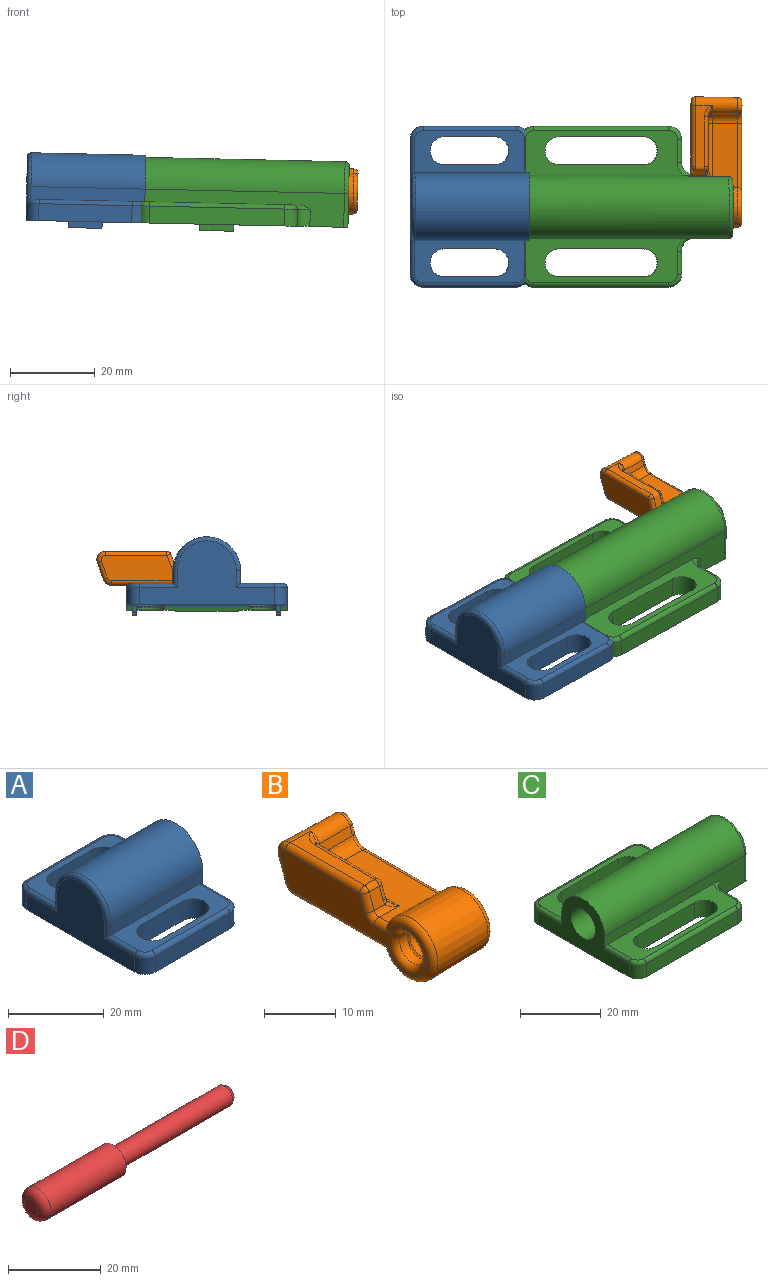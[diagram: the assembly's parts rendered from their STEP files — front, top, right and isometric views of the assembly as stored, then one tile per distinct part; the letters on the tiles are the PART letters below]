
ASSEMBLY  parts=4 mates=3
PART A: 46 faces, bbox 28.5x38.5x18.2 mm
  f0: plane 38x28mm, normal (0,0,-1), area 814.3mm2, adj f3,f4,f8,f9,f13,f14,f15,f16
  f1: plane 26x10mm, normal (0,0,1), area 144.9mm2, adj f5,f17,f18,f19,f20,f25,f26,f28
  f2: plane 26x10mm, normal (0,0,1), area 144.9mm2, adj f7,f13,f14,f15,f16,f27,f29,f31
  f3: plane 32x16mm, normal (1,0,0), area 215.6mm2, adj f0,f5,f6,f7,f12,f21,f23,f25
  f4: plane 22x4mm, normal (0,-1,0), area 88mm2, adj f0,f21,f22,f28
  f5: plane 27x4mm, normal (0,-1,0), area 81.2mm2, adj f1,f3,f6,f25,f34
  f6: cylinder r=8mm len=27mm, axis (1,0,0), area 678.6mm2, adj f3,f5,f7,f36
  f7: plane 27x4mm, normal (0,1,0), area 81.2mm2, adj f2,f3,f6,f27,f37
  f8: plane 22x4mm, normal (0,1,0), area 88mm2, adj f0,f23,f24,f31
  f9: plane 32x15mm, normal (-1,0,0), area 261mm2, adj f0,f22,f24,f32,f34,f35,f36,f37
  f10: plane 8.7x8.7mm, normal (1,0,0), area 59.4mm2, adj f11
  f11: cylinder r=4.35mm len=23.4mm, axis (1,0,0), area 639.6mm2, adj f10,f12
  f12: cone r=4.35mm half-angle=45deg, axis (1,0,0), area 24.8mm2, adj f3,f11
  f13: cylinder r=3.3mm len=6.6mm, axis (0,0,-1), area 51.8mm2, adj f0,f2,f14,f16
  f14: plane 12x5mm, normal (0,1,0), area 60mm2, adj f0,f2,f13,f15
  f15: cylinder r=3.3mm len=6.6mm, axis (0,0,-1), area 51.8mm2, adj f0,f2,f14,f16
  f16: plane 12x6.5mm, normal (0,-1,0), area 72mm2, adj f0,f2,f13,f15,f38,f39,f41
  f17: cylinder r=3.3mm len=6.6mm, axis (0,0,-1), area 51.8mm2, adj f0,f1,f18,f20
  f18: plane 12x6.5mm, normal (0,1,0), area 72mm2, adj f0,f1,f17,f19,f43,f44,f45
  f19: cylinder r=3.3mm len=6.6mm, axis (0,0,-1), area 51.8mm2, adj f0,f1,f18,f20
  f20: plane 12x5mm, normal (0,-1,0), area 60mm2, adj f0,f1,f17,f19
  f21: cylinder r=3mm len=4mm, axis (0,0,-1), area 18.8mm2, adj f0,f3,f4,f26
  f22: cylinder r=3mm len=4mm, axis (0,0,1), area 18.8mm2, adj f0,f4,f9,f30
  f23: cylinder r=3mm len=4mm, axis (0,0,1), area 18.8mm2, adj f0,f3,f8,f29
  f24: cylinder r=3mm len=4mm, axis (0,0,-1), area 18.8mm2, adj f0,f8,f9,f33
  f25: cylinder r=1mm len=8mm, axis (0,-1,0), area 12.6mm2, adj f1,f3,f5,f26
  f26: torus R=2mm, axis (0,0,1), area 6.5mm2, adj f1,f21,f25,f28
  f27: cylinder r=1mm len=8mm, axis (0,-1,0), area 12.6mm2, adj f2,f3,f7,f29
  f28: cylinder r=1mm len=22mm, axis (1,0,0), area 34.6mm2, adj f1,f4,f26,f30
  f29: torus R=2mm, axis (0,0,1), area 6.5mm2, adj f2,f23,f27,f31
  f30: torus R=2mm, axis (0,0,1), area 6.5mm2, adj f1,f22,f28,f32
  f31: cylinder r=1mm len=22mm, axis (1,0,0), area 34.6mm2, adj f2,f8,f29,f33
  f32: cylinder r=1mm len=9mm, axis (0,1,0), area 13.1mm2, adj f1,f9,f30,f34
  f33: torus R=2mm, axis (0,0,1), area 6.5mm2, adj f2,f24,f31,f35
  f34: cylinder r=1mm len=4mm, axis (0,0,1), area 5.3mm2, adj f5,f9,f32,f36
  f35: cylinder r=1mm len=9mm, axis (0,1,0), area 13.1mm2, adj f2,f9,f33,f37
  f36: torus R=7mm, axis (1,0,0), area 37.7mm2, adj f6,f9,f34,f37
  f37: cylinder r=1mm len=4mm, axis (0,0,-1), area 5.3mm2, adj f7,f9,f35,f36
  f38: plane 1.5x0.95mm, normal (1,0,0), area 1.4mm2, adj f0,f16,f40,f41
  f39: plane 1.5x0.95mm, normal (-1,0,0), area 1.4mm2, adj f0,f16,f40,f41
  f40: plane 8x1.5mm, normal (0,1,0), area 12mm2, adj f0,f38,f39,f41
  f41: plane 8x0.95mm, normal (0,0,-1), area 7.6mm2, adj f16,f38,f39,f40
  f42: plane 8x1.5mm, normal (0,-1,0), area 12mm2, adj f0,f43,f44,f45
  f43: plane 1.5x0.95mm, normal (-1,0,0), area 1.4mm2, adj f0,f18,f42,f45
  f44: plane 1.5x0.95mm, normal (1,0,0), area 1.4mm2, adj f0,f18,f42,f45
  f45: plane 8x0.95mm, normal (0,0,-1), area 7.6mm2, adj f18,f42,f43,f44
PART B: 50 faces, bbox 12x31.6x12.6 mm
  f0: plane 15.28x10.02mm, normal (0.02,0,1), area 100.1mm2, adj f1,f13,f17,f18,f25,f27,f48
  f1: cone r=5mm half-angle=1deg, axis (-1,0,0), area 269.9mm2, adj f0,f8,f23,f47
  f2: plane 4x4mm, normal (-1,0,0), area 12.6mm2, adj f3
  f3: cone r=2mm half-angle=2deg, axis (-1,0,0), area 96.9mm2, adj f2,f4
  f4: cone r=2.25mm half-angle=45deg, axis (-1,0,0), area 5.3mm2, adj f3,f5
  f5: cylinder r=2.5mm len=5mm, axis (-1,0,0), area 23.6mm2, adj f4,f49
  f6: plane 29x9mm, normal (-1,0,0), area 114.9mm2, adj f22,f23,f24,f25,f26,f27,f28,f29
  f7: plane 28.65x8.65mm, normal (1,0,0), area 85.9mm2, adj f41,f42,f43,f44,f45,f46,f47,f48
  f8: plane 18.08x10.02mm, normal (0.02,0,-1), area 180.5mm2, adj f1,f9,f22,f45
  f9: cone r=2mm half-angle=1deg, axis (-1,0,0), area 23.4mm2, adj f8,f10,f24,f43
  f10: plane 10.02x4.06mm, normal (0.02,0.94,-0.34), area 42.6mm2, adj f9,f11,f26,f41
  f11: cone r=2mm half-angle=1deg, axis (-1,0,0), area 50.6mm2, adj f10,f12,f16,f21,f28,f42
  f12: plane 6.04x1.4mm, normal (0.02,-0.94,0.34), area 8.8mm2, adj f11,f13,f20,f44
  f13: cone r=2mm half-angle=1deg, axis (1,0,0), area 15.6mm2, adj f0,f12,f19,f46
  f14: plane 2.72x2.13mm, normal (0.02,-0.94,0.34), area 5.8mm2, adj f17,f27,f29,f31,f35,f38,f39
  f15: plane 12.52x2.03mm, normal (1,0,0), area 23.9mm2, adj f18,f19,f20,f36,f38
  f16: plane 14.57x3.98mm, normal (0.02,0,1), area 31.1mm2, adj f11,f30,f31,f32,f34,f35,f36
  f17: cylinder r=1mm len=3.99mm, axis (-1,-0.01,0.02), area 3.6mm2, adj f0,f14,f27,f40
  f18: cylinder r=1mm len=13.12mm, axis (0,1,0), area 18.4mm2, adj f0,f15,f19,f39,f40
  f19: torus R=1.07mm, axis (1,0,0), area 3.2mm2, adj f13,f15,f18,f20
  f20: cylinder r=1mm len=1.71mm, axis (0,0.34,0.94), area 2.3mm2, adj f12,f15,f19,f21,f34
  f21: torus R=2.93mm, axis (1,0,0), area 1.4mm2, adj f11,f20,f32
  f22: cylinder r=1mm len=18.67mm, axis (0,1,0), area 28.6mm2, adj f6,f8,f23,f24
  f23: torus R=4mm, axis (-1,0,0), area 40.5mm2, adj f1,f6,f22,f25
  f24: torus R=1mm, axis (-1,0,0), area 3.1mm2, adj f6,f9,f22,f26
  f25: cylinder r=1mm len=2.7mm, axis (0,-1,0), area 3.5mm2, adj f0,f6,f23,f27
  f26: cylinder r=1mm len=4.34mm, axis (0,0.34,0.94), area 6.7mm2, adj f6,f10,f24,f28
  f27: torus R=2mm, axis (-1,0,0), area 2.6mm2, adj f0,f6,f14,f17,f25,f29
  f28: torus R=1mm, axis (-1,0,0), area 4.9mm2, adj f6,f11,f26,f30
  f29: cylinder r=1mm len=3.03mm, axis (0,-0.34,-0.94), area 4.5mm2, adj f6,f14,f27,f31
  f30: cylinder r=1mm len=14.57mm, axis (0,-1,0), area 22.9mm2, adj f6,f16,f28,f31
  f31: sphere r=1mm, area 1.2mm2, adj f14,f16,f29,f30,f33
  f32: bspline ~2.7x1.96mm, area 2.7mm2, adj f16,f21,f34
  f33: cylinder r=1mm len=0.94mm, axis (1,0,0), area 0mm2, adj f31,f35
  f34: bspline ~1x0.98mm, area 0.1mm2, adj f16,f20,f32,f36
  f35: cylinder r=1mm len=2.02mm, axis (-1,-0.01,0.02), area 2.5mm2, adj f14,f16,f33,f37
  f36: cylinder r=1mm len=11.78mm, axis (0,-1,0), area 18.3mm2, adj f15,f16,f34,f37
  f37: sphere r=1mm, area 1.2mm2, adj f35,f36,f38
  f38: cylinder r=1mm len=2.38mm, axis (0,-0.34,-0.94), area 3.4mm2, adj f14,f15,f37,f39
  f39: bspline ~1.17x1.04mm, area 0.8mm2, adj f14,f18,f38,f40
  f40: bspline ~1.91x1.91mm, area 1.4mm2, adj f17,f18,f39
  f41: cylinder r=1mm len=4.34mm, axis (0,0.34,0.94), area 6.6mm2, adj f7,f10,f42,f43
  f42: torus R=0.83mm, axis (1,0,0), area 7.1mm2, adj f7,f11,f41,f44
  f43: torus R=0.83mm, axis (1,0,0), area 2.8mm2, adj f7,f9,f41,f45
  f44: cylinder r=1mm len=1.71mm, axis (0,-0.34,-0.94), area 2.3mm2, adj f7,f12,f42,f46
  f45: cylinder r=1mm len=18.81mm, axis (0,1,0), area 28.5mm2, adj f7,f8,f43,f47
  f46: torus R=3.17mm, axis (1,0,0), area 4.8mm2, adj f7,f13,f44,f48
  f47: torus R=3.83mm, axis (1,0,0), area 38.9mm2, adj f1,f7,f45,f48
  f48: cylinder r=1mm len=16.01mm, axis (0,-1,0), area 24.1mm2, adj f0,f7,f46,f47
  f49: torus R=3.5mm, axis (-1,0,0), area 28.3mm2, adj f5,f6
PART C: 59 faces, bbox 50.2x38.5x17.6 mm
  f0: plane 50x38mm, normal (0,0,-1), area 1272.1mm2, adj f3,f5,f7,f8,f9,f10,f11,f12
  f1: plane 37.35x10.5mm, normal (0,0,1), area 211.3mm2, adj f9,f26,f27,f28,f29,f38,f39,f40
  f2: plane 37.35x10.5mm, normal (0,0,1), area 211.3mm2, adj f3,f22,f23,f24,f25,f44,f45,f46
  f3: plane 49x8mm, normal (0,1,0), area 164.3mm2, adj f0,f2,f4,f10,f17,f18,f19,f35
  f4: cylinder r=7.5mm len=49mm, axis (-1,0,0), area 1130.3mm2, adj f3,f9,f10,f19,f20,f21,f36
  f5: plane 14.5x13mm, normal (1,0,0), area 84.6mm2, adj f0,f6,f17,f21,f36,f37,f50
  f6: cylinder r=5mm len=15mm, axis (-1,0,0), area 417.1mm2, adj f5,f13,f17,f18,f19,f20,f21
  f7: plane 32x4mm, normal (0,-1,0), area 128mm2, adj f0,f31,f32,f40
  f8: plane 32x4mm, normal (0,1,0), area 128mm2, adj f0,f33,f34,f46
  f9: plane 49x8mm, normal (0,-1,0), area 188.2mm2, adj f0,f1,f4,f10,f30,f37,f38,f43
  f10: plane 32x15.5mm, normal (-1,0,0), area 219.6mm2, adj f0,f3,f4,f9,f16,f31,f33,f38
  f11: plane 5.5x4mm, normal (1,0,0), area 22mm2, adj f0,f34,f35,f48
  f12: plane 5.5x4mm, normal (1,0,0), area 22mm2, adj f0,f30,f32,f42
  f13: plane 10x10mm, normal (1,0,0), area 54.8mm2, adj f6,f14
  f14: cylinder r=2.75mm len=5.5mm, axis (-1,0,0), area 51.8mm2, adj f13,f15
  f15: plane 8.5x8.5mm, normal (-1,0,0), area 33mm2, adj f14,f16
  f16: cylinder r=4.25mm len=32mm, axis (-1,0,0), area 854.5mm2, adj f10,f15
  f17: plane 10x3.04mm, normal (0,0,1), area 30.1mm2, adj f3,f5,f6,f18,f50
  f18: cylinder r=2mm len=3.04mm, axis (0,-1,0), area 8.7mm2, adj f3,f6,f17,f19
  f19: plane 2.51x0.5mm, normal (1,0,0), area 1.3mm2, adj f3,f4,f6,f18,f20
  f20: cylinder r=2mm len=3.03mm, axis (0,-1,0), area 8.2mm2, adj f4,f6,f19,f21
  f21: plane 10x2.69mm, normal (0,0,-1), area 26.7mm2, adj f4,f5,f6,f20,f36
  f22: cylinder r=3.3mm len=6.6mm, axis (0,0,-1), area 51.8mm2, adj f0,f2,f23,f25
  f23: plane 20x5mm, normal (0,1,0), area 100mm2, adj f0,f2,f22,f24
  f24: cylinder r=3.3mm len=6.6mm, axis (0,0,-1), area 51.8mm2, adj f0,f2,f23,f25
  f25: plane 20x6.5mm, normal (0,-1,0), area 112mm2, adj f0,f2,f22,f24,f51,f52,f54
  f26: cylinder r=3.3mm len=6.6mm, axis (0,0,-1), area 51.8mm2, adj f0,f1,f27,f29
  f27: plane 20x6.5mm, normal (0,1,0), area 112mm2, adj f0,f1,f26,f28,f56,f57,f58
  f28: cylinder r=3.3mm len=6.6mm, axis (0,0,-1), area 51.8mm2, adj f0,f1,f27,f29
  f29: plane 20x5mm, normal (0,-1,0), area 100mm2, adj f0,f1,f26,f28
  f30: cylinder r=3mm len=4mm, axis (0,0,1), area 18.8mm2, adj f0,f9,f12,f43
  f31: cylinder r=3mm len=4mm, axis (0,0,-1), area 18.8mm2, adj f0,f7,f10,f39
  f32: cylinder r=3mm len=4mm, axis (0,0,1), area 18.8mm2, adj f0,f7,f12,f41
  f33: cylinder r=3mm len=4mm, axis (0,0,1), area 18.8mm2, adj f0,f8,f10,f45
  f34: cylinder r=3mm len=4mm, axis (0,0,1), area 18.8mm2, adj f0,f8,f11,f47
  f35: cylinder r=3mm len=4mm, axis (0,0,1), area 18.8mm2, adj f0,f3,f11,f49
  f36: torus R=6.5mm, axis (1,0,0), area 31.6mm2, adj f4,f5,f21,f37
  f37: cylinder r=1mm len=8mm, axis (0,0,1), area 12.6mm2, adj f0,f5,f9,f36
  f38: cylinder r=1mm len=8.5mm, axis (0,-1,0), area 13.4mm2, adj f1,f9,f10,f39
  f39: torus R=2mm, axis (0,0,-1), area 6.5mm2, adj f1,f31,f38,f40
  f40: cylinder r=1mm len=32mm, axis (-1,0,0), area 50.3mm2, adj f1,f7,f39,f41
  f41: torus R=2mm, axis (0,0,-1), area 6.5mm2, adj f1,f32,f40,f42
  f42: cylinder r=1mm len=5.5mm, axis (0,1,0), area 8.6mm2, adj f1,f12,f41,f43
  f43: torus R=4mm, axis (0,0,-1), area 6.1mm2, adj f1,f9,f30,f42
  f44: cylinder r=1mm len=8.5mm, axis (0,-1,0), area 13.4mm2, adj f2,f3,f10,f45
  f45: torus R=2mm, axis (0,0,-1), area 6.5mm2, adj f2,f33,f44,f46
  f46: cylinder r=1mm len=32mm, axis (-1,0,0), area 50.3mm2, adj f2,f8,f45,f47
  f47: torus R=2mm, axis (0,0,-1), area 6.5mm2, adj f2,f34,f46,f48
  f48: cylinder r=1mm len=5.5mm, axis (0,-1,0), area 8.6mm2, adj f2,f11,f47,f49
  f49: torus R=4mm, axis (0,0,-1), area 6.1mm2, adj f2,f3,f35,f48
  f50: cylinder r=1mm len=5.75mm, axis (0,0,-1), area 9mm2, adj f0,f3,f5,f17
  f51: plane 1.5x0.95mm, normal (1,0,0), area 1.4mm2, adj f0,f25,f53,f54
  f52: plane 1.5x0.95mm, normal (-1,0,0), area 1.4mm2, adj f0,f25,f53,f54
  f53: plane 8x1.5mm, normal (0,1,0), area 12mm2, adj f0,f51,f52,f54
  f54: plane 8x0.95mm, normal (0,0,-1), area 7.6mm2, adj f25,f51,f52,f53
  f55: plane 8x1.5mm, normal (0,-1,0), area 12mm2, adj f0,f56,f57,f58
  f56: plane 1.5x0.95mm, normal (-1,0,0), area 1.4mm2, adj f0,f27,f55,f58
  f57: plane 1.5x0.95mm, normal (1,0,0), area 1.4mm2, adj f0,f27,f55,f58
  f58: plane 8x0.95mm, normal (0,0,-1), area 7.6mm2, adj f27,f55,f56,f57
PART D: 7 faces, bbox 60x8.7x8.7 mm
  f0: plane 4x4mm, normal (-1,0,0), area 12.6mm2, adj f1
  f1: torus R=2mm, axis (-1,0,0), area 64.6mm2, adj f0,f2
  f2: cylinder r=4mm len=23mm, axis (-1,0,0), area 578.1mm2, adj f1,f3
  f3: plane 8x8mm, normal (1,0,0), area 30.6mm2, adj f2,f4
  f4: cylinder r=2.5mm len=34.13mm, axis (-1,0,0), area 536.2mm2, adj f3,f5
  f5: cone r=2mm half-angle=30deg, axis (-1,0,0), area 14.1mm2, adj f4,f6
  f6: plane 4x4mm, normal (1,0,0), area 12.6mm2, adj f5
PLACE A rot(axis=(0,1,0),1.2deg) t=(-25.86,31.28,-21.23)mm
PLACE B rot(axis=(0,1,0),1.2deg) t=(-45.61,31.28,-20.8)mm
PLACE C rot(axis=(0,1,0),1.2deg) t=(-47.72,31.28,-20.75)mm
PLACE D rot(axis=(0,1,0),1.2deg) t=(-45.61,31.28,-20.8)mm
MATE slider D.f1 <-> C.f6  axis (-1,0,0.02) through (-23.94,31.28,-13.27)mm
MATE slider D.f1 <-> A.f6  axis (-1,0,0.02) through (-37.44,31.28,-12.98)mm
MATE fastened D.f1 <-> B.f1  axis (1,0,-0.02) through (22.55,31.28,-14.28)mm
